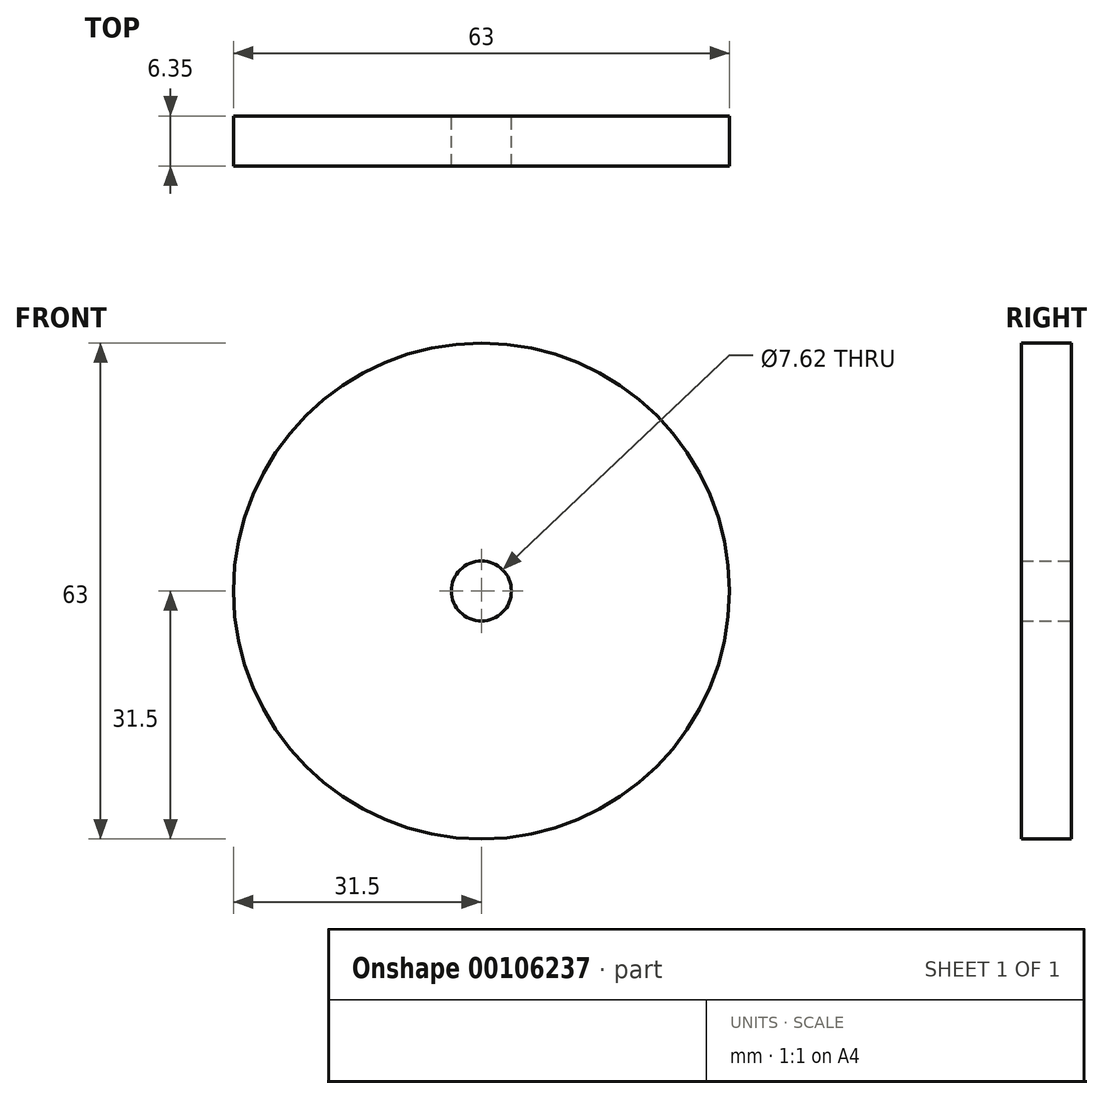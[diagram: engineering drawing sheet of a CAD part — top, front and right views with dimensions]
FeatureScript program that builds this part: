
annotation { "Feature Type Name" : "Feature", "Feature Type Description" : "" }
export const myFeature = defineFeature(function(context is Context, id is Id, definition is map)
    precondition{}
    {
        {
            var Q0;
            Q0=qCreatedBy(makeId("Front.planeOp"),FACE);
            var sketch = newSketch(context, id + "F0", { "sketchPlane" : qUnion([Q0])});
            skCircle(sketch, "E0", {"center": v(0, 0) * mm, "radius": 3.81 * mm});
            skCircle(sketch, "E1", {"center": v(0, 0) * mm, "radius": 31.5 * mm});
            skSolve(sketch);
        }
        {
            var Q0;
            Q0=makeQuery(id+"F0.imprint","IMPRINT",FACE,{"disambiguationData":[TD([[makeQuery(id+"F0.imprint","IMPRINT",EDGE,{"derivedFrom":sQuery(id+"F0.wireOp",EDGE,"E0")}),-1.0]])]});
            extrude(context, id + "F1", {"entities" : qUnion([Q0]), "depth" : 6.35 * mm});
        }
    });
